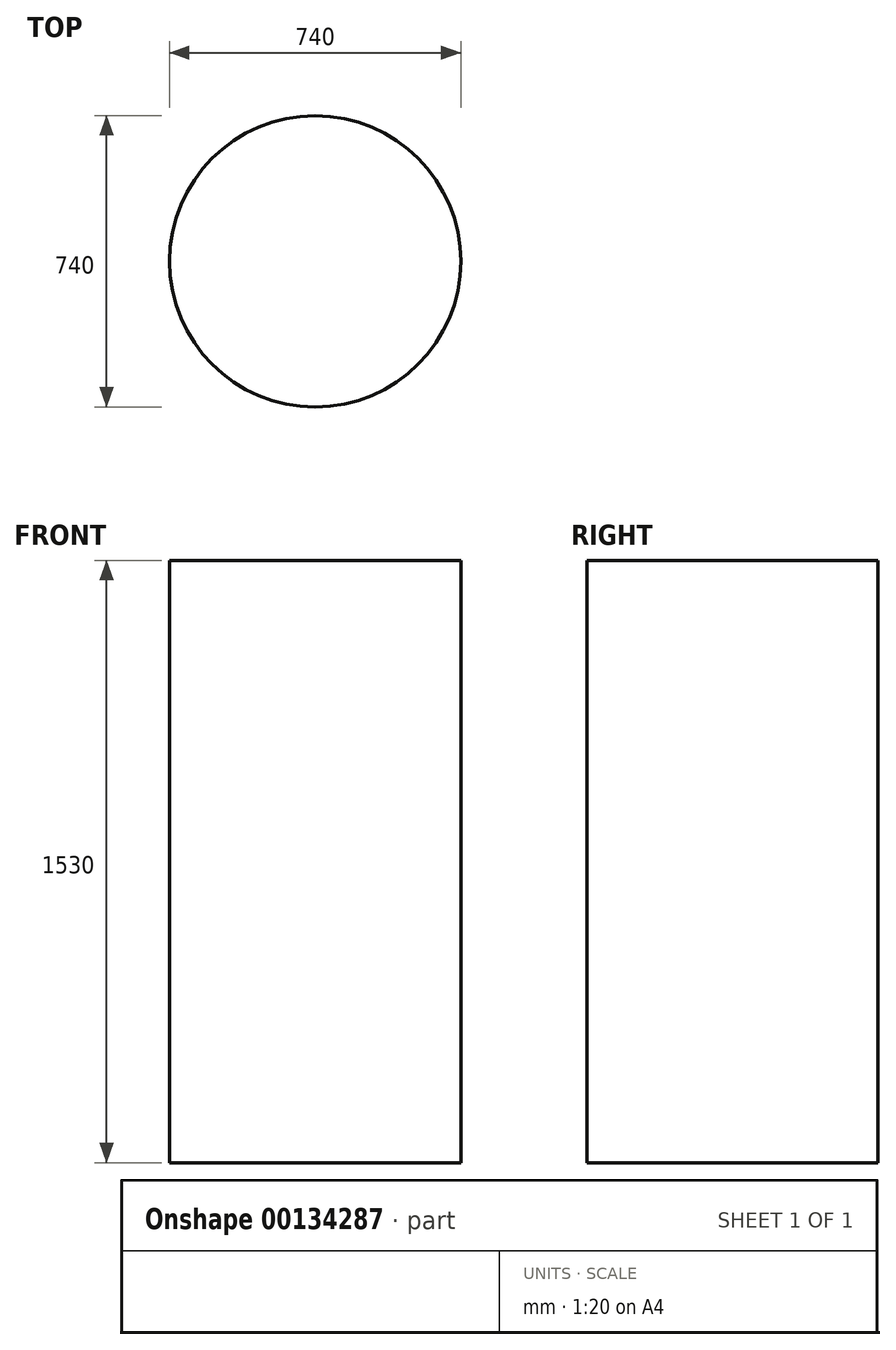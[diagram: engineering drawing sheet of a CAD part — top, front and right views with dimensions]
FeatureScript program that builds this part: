
annotation { "Feature Type Name" : "Feature", "Feature Type Description" : "" }
export const myFeature = defineFeature(function(context is Context, id is Id, definition is map)
    precondition{}
    {
        {
            var Q0;
            Q0=qCreatedBy(makeId("Top.planeOp"),FACE);
            var sketch = newSketch(context, id + "F0", { "sketchPlane" : qUnion([Q0])});
            skCircle(sketch, "E0", {"center": v(0, 0) * mm, "radius": 370 * mm});
            skSolve(sketch);
        }
        {
            var Q0;
            Q0 = qSketchRegion(id + "F0", true);
            extrude(context, id + "F1", {"entities" : qUnion([Q0]), "depth" : 1530 * mm});
        }
    });
